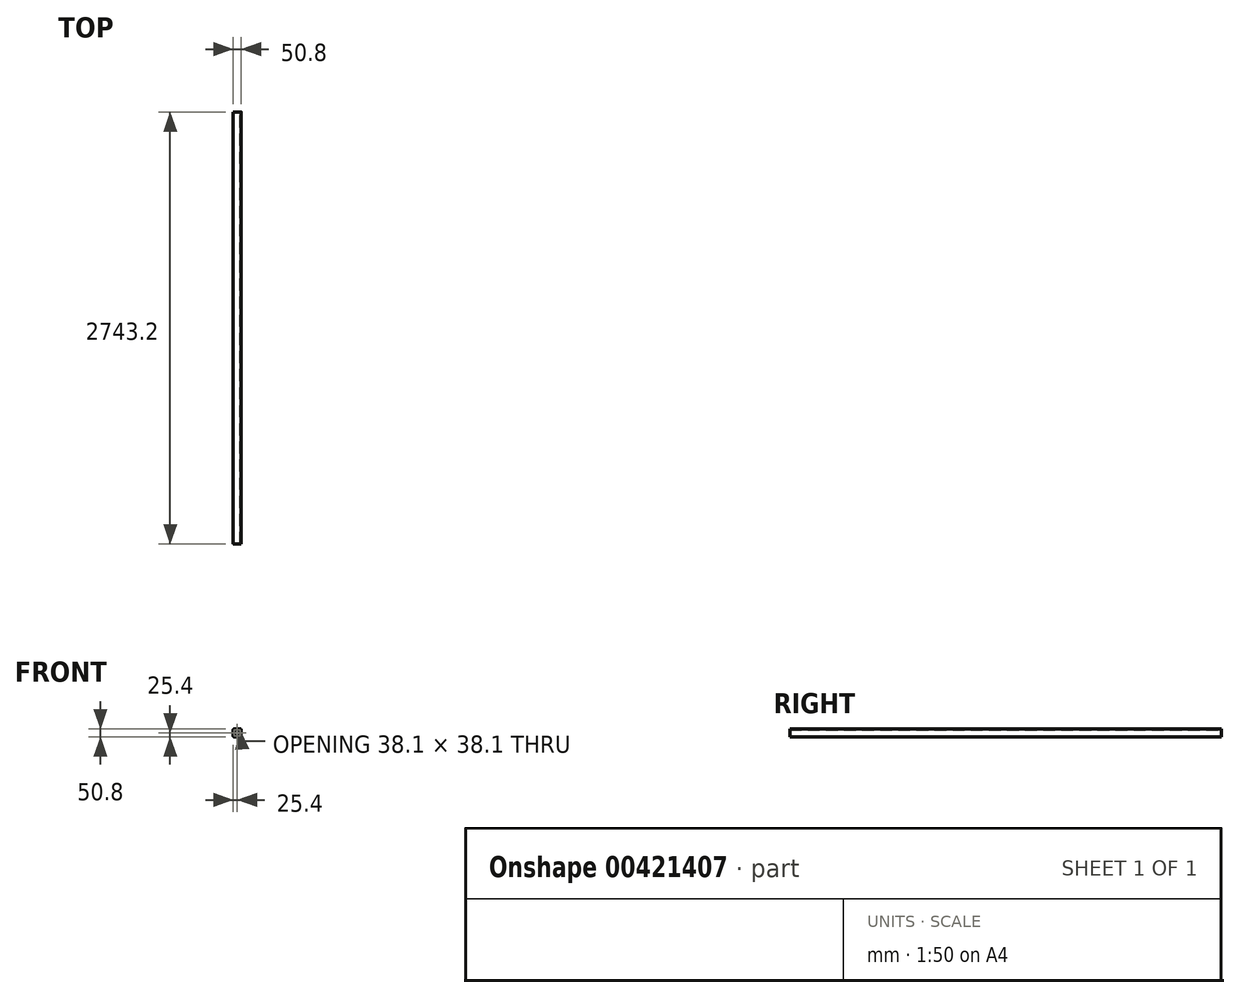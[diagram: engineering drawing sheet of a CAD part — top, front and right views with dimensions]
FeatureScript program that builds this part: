
annotation { "Feature Type Name" : "Feature", "Feature Type Description" : "" }
export const myFeature = defineFeature(function(context is Context, id is Id, definition is map)
    precondition{}
    {
        {
            var Q0;
            Q0=qCreatedBy(makeId("Front.planeOp"),FACE);
            var sketch = newSketch(context, id + "F0", { "sketchPlane" : qUnion([Q0])});
            skLineSegment(sketch, "E0.bottom", {"start": v(19.05, -19.05) * mm, "end": v(-19.05, -19.05) * mm});
            skLineSegment(sketch, "E0.top", {"start": v(19.05, 19.05) * mm, "end": v(-19.05, 19.05) * mm});
            skLineSegment(sketch, "E0.left", {"start": v(19.05, -19.05) * mm, "end": v(19.05, 19.05) * mm});
            skLineSegment(sketch, "E0.right", {"start": v(-19.05, -19.05) * mm, "end": v(-19.05, 19.05) * mm});
            skPoint(sketch, "E0.middle", {"position": v(0, 0) * mm});
            skLineSegment(sketch, "E1.bottom", {"start": v(25.4, -25.4) * mm, "end": v(-25.4, -25.4) * mm});
            skLineSegment(sketch, "E1.top", {"start": v(25.4, 25.4) * mm, "end": v(-25.4, 25.4) * mm});
            skLineSegment(sketch, "E1.left", {"start": v(25.4, -25.4) * mm, "end": v(25.4, 25.4) * mm});
            skLineSegment(sketch, "E1.right", {"start": v(-25.4, -25.4) * mm, "end": v(-25.4, 25.4) * mm});
            skSolve(sketch);
        }
        {
            var Q0;
            Q0 = qSketchRegion(id + "F0", true);
            extrude(context, id + "F1", {"entities" : qUnion([Q0]), "endBound" : BoundingType.SYMMETRIC, "depth" : 2743.2 * mm});
        }
        {
            var Q0;
            Q0=makeQuery(id+"F1.opExtrude","SWEPT_EDGE",EDGE,{"disambiguationData":[OSD([sQuery(id+"F0.wireOp",EDGE,"E1.top"),sQuery(id+"F0.wireOp",EDGE,"E1.right")])]});
            var Q1;
            Q1=makeQuery(id+"F1.opExtrude","SWEPT_EDGE",EDGE,{"disambiguationData":[OSD([sQuery(id+"F0.wireOp",EDGE,"E1.top"),sQuery(id+"F0.wireOp",EDGE,"E1.left")])]});
            var Q2;
            Q2=makeQuery(id+"F1.opExtrude","SWEPT_EDGE",EDGE,{"disambiguationData":[OSD([sQuery(id+"F0.wireOp",EDGE,"E0.bottom"),sQuery(id+"F0.wireOp",EDGE,"E0.left")])]});
            var Q3;
            Q3=makeQuery(id+"F1.opExtrude","SWEPT_EDGE",EDGE,{"disambiguationData":[OSD([sQuery(id+"F0.wireOp",EDGE,"E0.bottom"),sQuery(id+"F0.wireOp",EDGE,"E0.right")])]});
            var Q4;
            Q4=makeQuery(id+"F1.opExtrude","SWEPT_EDGE",EDGE,{"disambiguationData":[OSD([sQuery(id+"F0.wireOp",EDGE,"E1.bottom"),sQuery(id+"F0.wireOp",EDGE,"E1.left")])]});
            var Q5;
            Q5=makeQuery(id+"F1.opExtrude","SWEPT_EDGE",EDGE,{"disambiguationData":[OSD([sQuery(id+"F0.wireOp",EDGE,"E1.bottom"),sQuery(id+"F0.wireOp",EDGE,"E1.right")])]});
            var Q6;
            Q6=makeQuery(id+"F1.opExtrude","SWEPT_EDGE",EDGE,{"disambiguationData":[OSD([sQuery(id+"F0.wireOp",EDGE,"E0.top"),sQuery(id+"F0.wireOp",EDGE,"E0.left")])]});
            var Q7;
            Q7=makeQuery(id+"F1.opExtrude","SWEPT_EDGE",EDGE,{"disambiguationData":[OSD([sQuery(id+"F0.wireOp",EDGE,"E0.top"),sQuery(id+"F0.wireOp",EDGE,"E0.right")])]});
            fillet(context, id + "F2", {"entities" : qUnion([Q0, Q1, Q2, Q3, Q4, Q5, Q6, Q7]), "radius" : 6.35 * mm, "tangentPropagation" : true, "allowEdgeOverflow" : false});
        }
    });
